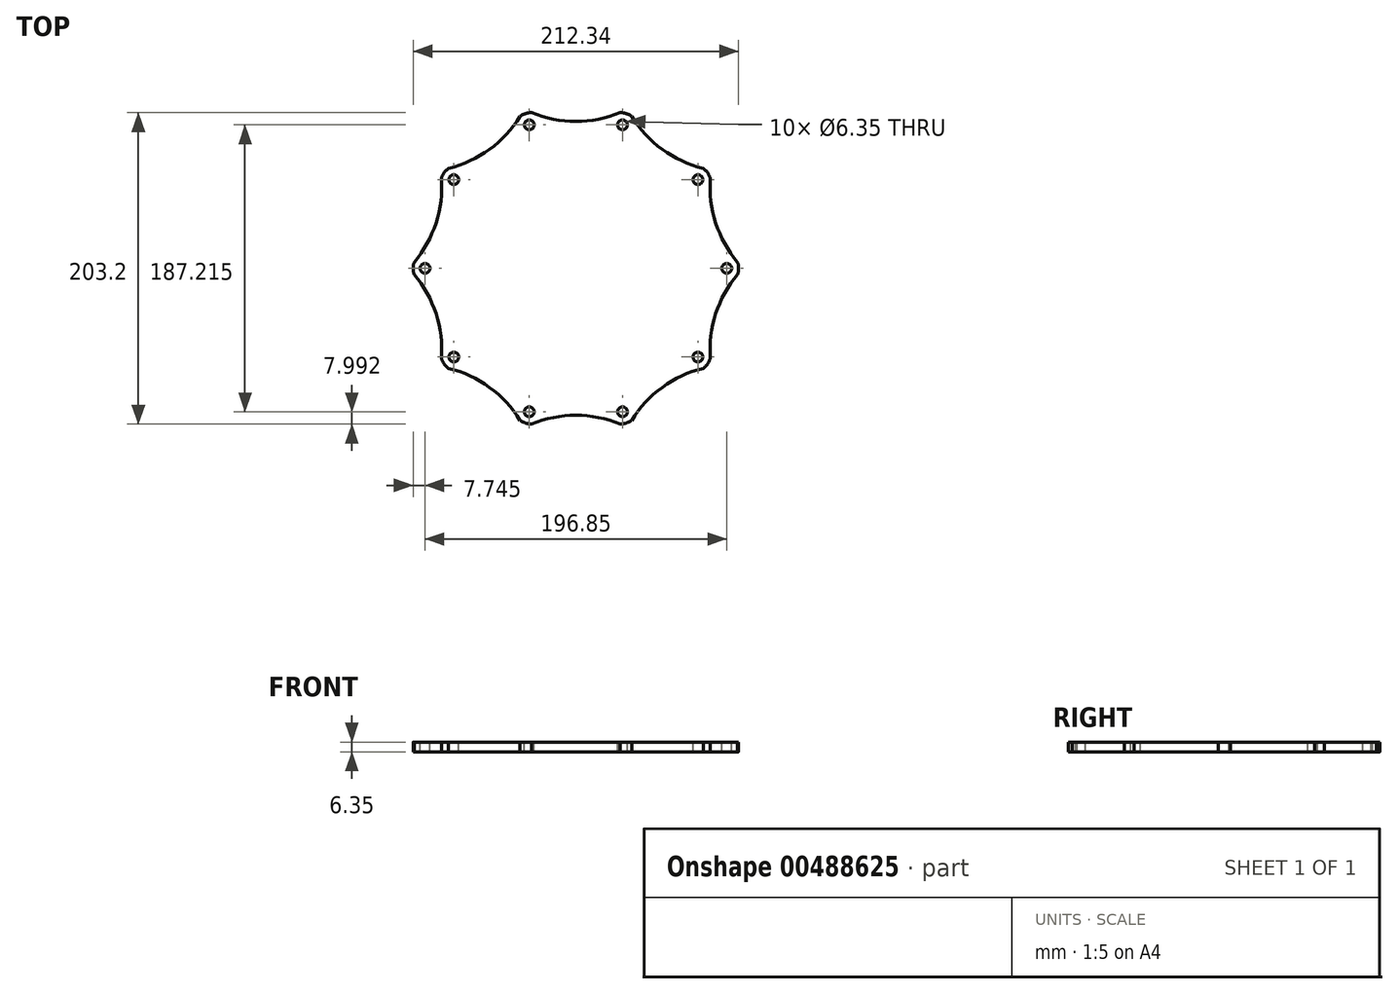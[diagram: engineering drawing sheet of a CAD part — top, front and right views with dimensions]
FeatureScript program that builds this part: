
annotation { "Feature Type Name" : "Feature", "Feature Type Description" : "" }
export const myFeature = defineFeature(function(context is Context, id is Id, definition is map)
    precondition{}
    {
        {
            var Q0;
            Q0=qCreatedBy(makeId("Top.planeOp"),FACE);
            var sketch = newSketch(context, id + "F0", { "sketchPlane" : qUnion([Q0])});
            skCircle(sketch, "E0.cCircle", {"center": v(0, 0) * mm, "radius": 101.6 * mm, "construction": true});
            skLineSegment(sketch, "E0.0", {"start": v(-33.01, 101.6) * mm, "end": v(33.01, 101.6) * mm});
            skLineSegment(sketch, "E0.1", {"start": v(33.01, 101.6) * mm, "end": v(86.43, 62.8) * mm});
            skLineSegment(sketch, "E0.2", {"start": v(86.43, 62.8) * mm, "end": v(106.83, 0) * mm});
            skLineSegment(sketch, "E0.3", {"start": v(106.83, 0) * mm, "end": v(86.43, -62.8) * mm});
            skLineSegment(sketch, "E0.4", {"start": v(86.43, -62.8) * mm, "end": v(33.01, -101.6) * mm});
            skLineSegment(sketch, "E0.5", {"start": v(33.01, -101.6) * mm, "end": v(-33.01, -101.6) * mm});
            skLineSegment(sketch, "E0.6", {"start": v(-33.01, -101.6) * mm, "end": v(-86.43, -62.8) * mm});
            skLineSegment(sketch, "E0.7", {"start": v(-86.43, -62.8) * mm, "end": v(-106.83, 0) * mm});
            skLineSegment(sketch, "E0.8", {"start": v(-106.83, 0) * mm, "end": v(-86.43, 62.8) * mm});
            skLineSegment(sketch, "E0.9", {"start": v(-86.43, 62.8) * mm, "end": v(-33.01, 101.6) * mm});
            skPoint(sketch, "E0.0.midPoint", {"position": v(0, 101.6) * mm});
            skSolve(sketch);
        }
        {
            var Q0;
            Q0 = qSketchRegion(id + "F0", true);
            extrude(context, id + "F1", {"entities" : qUnion([Q0]), "depth" : 6.35 * mm});
        }
        {
            var Q0;
            Q0=makeQuery(id+"F1.opExtrude","CAP_FACE",FACE,{"disambiguationData":[OSD([sQuery(id+"F0.wireOp",EDGE,"E0.0"),sQuery(id+"F0.wireOp",EDGE,"E0.1"),sQuery(id+"F0.wireOp",EDGE,"E0.2"),sQuery(id+"F0.wireOp",EDGE,"E0.3"),sQuery(id+"F0.wireOp",EDGE,"E0.4"),sQuery(id+"F0.wireOp",EDGE,"E0.5"),sQuery(id+"F0.wireOp",EDGE,"E0.6"),sQuery(id+"F0.wireOp",EDGE,"E0.7"),sQuery(id+"F0.wireOp",EDGE,"E0.8"),sQuery(id+"F0.wireOp",EDGE,"E0.9")])],"isStart":false});
            var sketch = newSketch(context, id + "F2", { "sketchPlane" : qUnion([Q0])});
            skCircle(sketch, "E1", {"center": v(0, 0) * mm, "radius": 98.43 * mm, "construction": true});
            skLineSegment(sketch, "E2", {"start": v(0, 0) * mm, "end": v(-33.01, 101.6) * mm, "construction": true});
            skCircle(sketch, "E3", {"center": v(-30.41, 93.6) * mm, "radius": 3.18 * mm});
            skCircle(sketch, "E4.1.0", {"center": v(-79.63, 57.85) * mm, "radius": 3.18 * mm});
            skCircle(sketch, "E4.2.0", {"center": v(-98.43, 0) * mm, "radius": 3.18 * mm});
            skCircle(sketch, "E4.3.0", {"center": v(-79.63, -57.85) * mm, "radius": 3.18 * mm});
            skCircle(sketch, "E4.4.0", {"center": v(-30.41, -93.6) * mm, "radius": 3.18 * mm});
            skCircle(sketch, "E4.5.0", {"center": v(30.41, -93.6) * mm, "radius": 3.18 * mm});
            skCircle(sketch, "E4.6.0", {"center": v(79.63, -57.85) * mm, "radius": 3.18 * mm});
            skCircle(sketch, "E4.7.0", {"center": v(98.43, 0) * mm, "radius": 3.18 * mm});
            skCircle(sketch, "E4.8.0", {"center": v(79.63, 57.85) * mm, "radius": 3.18 * mm});
            skCircle(sketch, "E4.9.0", {"center": v(30.41, 93.6) * mm, "radius": 3.18 * mm});
            skSolve(sketch);
        }
        {
            var Q0;
            Q0 = qSketchRegion(id + "F2", true);
            extrude(context, id + "F3", {"entities" : qUnion([Q0]), "operationType" : NewBodyOperationType.REMOVE, "endBound" : BoundingType.UP_TO_NEXT, "oppositeDirection" : true, "depth" : 25.4 * mm});
        }
        {
            var Q0;
            Q0=makeQuery(id+"F1.opExtrude","SWEPT_EDGE",EDGE,{"disambiguationData":[OSD([sQuery(id+"F0.wireOp",EDGE,"E0.8"),sQuery(id+"F0.wireOp",EDGE,"E0.9")])]});
            var Q1;
            Q1=makeQuery(id+"F1.opExtrude","SWEPT_EDGE",EDGE,{"disambiguationData":[OSD([sQuery(id+"F0.wireOp",EDGE,"E0.7"),sQuery(id+"F0.wireOp",EDGE,"E0.8")])]});
            var Q2;
            Q2=makeQuery(id+"F1.opExtrude","SWEPT_EDGE",EDGE,{"disambiguationData":[OSD([sQuery(id+"F0.wireOp",EDGE,"E0.6"),sQuery(id+"F0.wireOp",EDGE,"E0.7")])]});
            var Q3;
            Q3=makeQuery(id+"F1.opExtrude","SWEPT_EDGE",EDGE,{"disambiguationData":[OSD([sQuery(id+"F0.wireOp",EDGE,"E0.5"),sQuery(id+"F0.wireOp",EDGE,"E0.6")])]});
            var Q4;
            Q4=makeQuery(id+"F1.opExtrude","SWEPT_EDGE",EDGE,{"disambiguationData":[OSD([sQuery(id+"F0.wireOp",EDGE,"E0.4"),sQuery(id+"F0.wireOp",EDGE,"E0.5")])]});
            var Q5;
            Q5=makeQuery(id+"F1.opExtrude","SWEPT_EDGE",EDGE,{"disambiguationData":[OSD([sQuery(id+"F0.wireOp",EDGE,"E0.3"),sQuery(id+"F0.wireOp",EDGE,"E0.4")])]});
            var Q6;
            Q6=makeQuery(id+"F1.opExtrude","SWEPT_EDGE",EDGE,{"disambiguationData":[OSD([sQuery(id+"F0.wireOp",EDGE,"E0.2"),sQuery(id+"F0.wireOp",EDGE,"E0.3")])]});
            var Q7;
            Q7=makeQuery(id+"F1.opExtrude","SWEPT_EDGE",EDGE,{"disambiguationData":[OSD([sQuery(id+"F0.wireOp",EDGE,"E0.0"),sQuery(id+"F0.wireOp",EDGE,"E0.1")])]});
            var Q8;
            Q8=makeQuery(id+"F1.opExtrude","SWEPT_EDGE",EDGE,{"disambiguationData":[OSD([sQuery(id+"F0.wireOp",EDGE,"E0.1"),sQuery(id+"F0.wireOp",EDGE,"E0.2")])]});
            var Q9;
            Q9=makeQuery(id+"F1.opExtrude","SWEPT_EDGE",EDGE,{"disambiguationData":[OSD([sQuery(id+"F0.wireOp",EDGE,"E0.0"),sQuery(id+"F0.wireOp",EDGE,"E0.9")])]});
            fillet(context, id + "F4", {"entities" : qUnion([Q0, Q1, Q2, Q3, Q4, Q5, Q6, Q7, Q8, Q9]), "radius" : 12.7 * mm, "tangentPropagation" : true, "allowEdgeOverflow" : false});
        }
        {
            var Q0;
            Q0=makeQuery(id+"F1.opExtrude","CAP_FACE",FACE,{"disambiguationData":[OSD([sQuery(id+"F0.wireOp",EDGE,"E0.0"),sQuery(id+"F0.wireOp",EDGE,"E0.1"),sQuery(id+"F0.wireOp",EDGE,"E0.2"),sQuery(id+"F0.wireOp",EDGE,"E0.3"),sQuery(id+"F0.wireOp",EDGE,"E0.4"),sQuery(id+"F0.wireOp",EDGE,"E0.5"),sQuery(id+"F0.wireOp",EDGE,"E0.6"),sQuery(id+"F0.wireOp",EDGE,"E0.7"),sQuery(id+"F0.wireOp",EDGE,"E0.8"),sQuery(id+"F0.wireOp",EDGE,"E0.9")])],"isStart":false});
            var sketch = newSketch(context, id + "F5", { "sketchPlane" : qUnion([Q0])});
            skArc(sketch, "E5", {"start": v(-28.89, 101.6) * mm, "mid": v(0, 95.91) * mm, "end": v(28.89, 101.6) * mm});
            skLineSegment(sketch, "E6", {"start": v(-28.89, 101.6) * mm, "end": v(28.89, 101.6) * mm});
            skArc(sketch, "E7.1.0", {"start": v(-83.09, 65.22) * mm, "mid": v(-56.38, 77.6) * mm, "end": v(-36.35, 99.17) * mm});
            skLineSegment(sketch, "E7.1.1", {"start": v(-83.09, 65.22) * mm, "end": v(-36.35, 99.17) * mm});
            skArc(sketch, "E7.2.0", {"start": v(-105.55, 3.92) * mm, "mid": v(-91.22, 29.64) * mm, "end": v(-87.7, 58.87) * mm});
            skLineSegment(sketch, "E7.2.1", {"start": v(-105.55, 3.92) * mm, "end": v(-87.7, 58.87) * mm});
            skArc(sketch, "E7.3.0", {"start": v(-87.7, -58.87) * mm, "mid": v(-91.22, -29.64) * mm, "end": v(-105.55, -3.92) * mm});
            skLineSegment(sketch, "E7.3.1", {"start": v(-87.7, -58.87) * mm, "end": v(-105.55, -3.92) * mm});
            skArc(sketch, "E7.4.0", {"start": v(-36.35, -99.17) * mm, "mid": v(-56.38, -77.6) * mm, "end": v(-83.09, -65.22) * mm});
            skLineSegment(sketch, "E7.4.1", {"start": v(-36.35, -99.17) * mm, "end": v(-83.09, -65.22) * mm});
            skArc(sketch, "E7.5.0", {"start": v(28.89, -101.6) * mm, "mid": v(0, -95.91) * mm, "end": v(-28.89, -101.6) * mm});
            skLineSegment(sketch, "E7.5.1", {"start": v(28.89, -101.6) * mm, "end": v(-28.89, -101.6) * mm});
            skArc(sketch, "E7.6.0", {"start": v(83.09, -65.22) * mm, "mid": v(56.38, -77.6) * mm, "end": v(36.35, -99.17) * mm});
            skLineSegment(sketch, "E7.6.1", {"start": v(83.09, -65.22) * mm, "end": v(36.35, -99.17) * mm});
            skArc(sketch, "E7.7.0", {"start": v(105.55, -3.92) * mm, "mid": v(91.22, -29.64) * mm, "end": v(87.7, -58.87) * mm});
            skLineSegment(sketch, "E7.7.1", {"start": v(105.55, -3.92) * mm, "end": v(87.7, -58.87) * mm});
            skArc(sketch, "E7.8.0", {"start": v(87.7, 58.87) * mm, "mid": v(91.22, 29.64) * mm, "end": v(105.55, 3.92) * mm});
            skLineSegment(sketch, "E7.8.1", {"start": v(87.7, 58.87) * mm, "end": v(105.55, 3.92) * mm});
            skArc(sketch, "E7.9.0", {"start": v(36.35, 99.17) * mm, "mid": v(56.38, 77.6) * mm, "end": v(83.09, 65.22) * mm});
            skLineSegment(sketch, "E7.9.1", {"start": v(36.35, 99.17) * mm, "end": v(83.09, 65.22) * mm});
            skPoint(sketch, "E7.center", {"position": v(0, 0) * mm});
            skSolve(sketch);
        }
        {
            var Q0;
            Q0 = qSketchRegion(id + "F5", true);
            extrude(context, id + "F6", {"entities" : qUnion([Q0]), "operationType" : NewBodyOperationType.REMOVE, "endBound" : BoundingType.UP_TO_NEXT, "oppositeDirection" : true, "depth" : 25.4 * mm});
        }
    });
